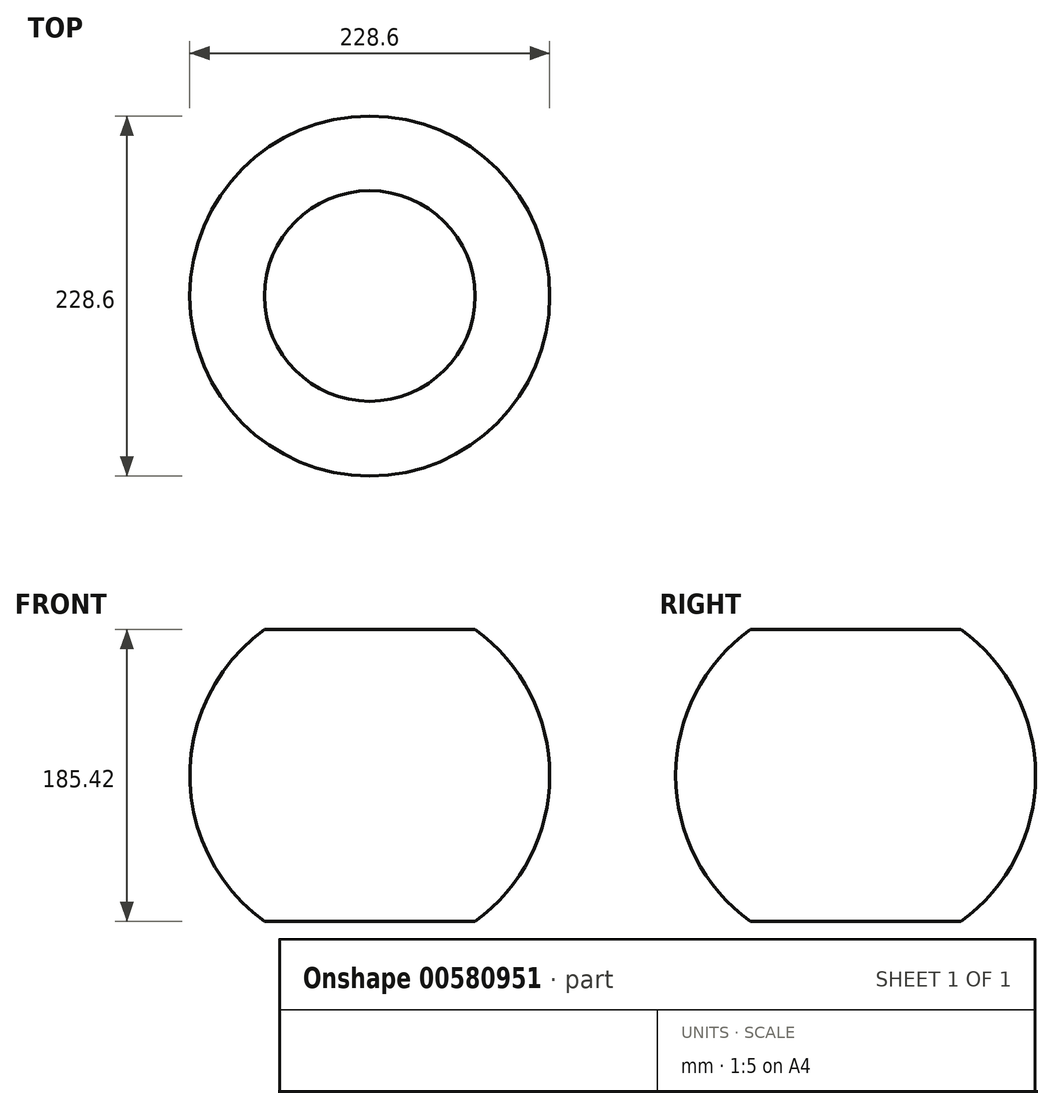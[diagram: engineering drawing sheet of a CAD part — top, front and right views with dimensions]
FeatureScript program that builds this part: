
annotation { "Feature Type Name" : "Feature", "Feature Type Description" : "" }
export const myFeature = defineFeature(function(context is Context, id is Id, definition is map)
    precondition{}
    {
        {
            var Q0;
            Q0=qCreatedBy(makeId("Front.planeOp"),FACE);
            var sketch = newSketch(context, id + "F0", { "sketchPlane" : qUnion([Q0])});
            skArc(sketch, "E0", {"start": v(0, -114.3) * mm, "mid": v(114.3, 0) * mm, "end": v(0, 114.3) * mm});
            skLineSegment(sketch, "E1", {"start": v(0, 114.3) * mm, "end": v(0, -114.3) * mm});
            skSolve(sketch);
        }
        {
            var Q0;
            Q0=makeQuery(id+"F0.imprint","IMPRINT",FACE,{"disambiguationData":[TD([[makeQuery(id+"F0.imprint","IMPRINT",EDGE,{"derivedFrom":sQuery(id+"F0.wireOp",EDGE,"E0")}),1.0]])]});
            var Q1;
            Q1=sQuery(id+"F0.wireOp",EDGE,"E0");
            var Q2;
            Q2=sQuery(id+"F0.wireOp",EDGE,"E1");
            revolve(context, id + "F1", {"entities" : qUnion([Q0]), "surfaceEntities" : qUnion([Q1]), "axis" : qUnion([Q2]), "revolveType" : RevolveType.FULL});
        }
        {
            var Q0;
            Q0=qCreatedBy(makeId("Front.planeOp"),FACE);
            var sketch = newSketch(context, id + "F2", { "sketchPlane" : qUnion([Q0])});
            skLineSegment(sketch, "E2.bottom", {"start": v(-129.8, 129.8) * mm, "end": v(129.8, 129.8) * mm});
            skLineSegment(sketch, "E2.top", {"start": v(-129.8, 92.7) * mm, "end": v(129.8, 92.7) * mm});
            skLineSegment(sketch, "E2.left", {"start": v(-129.8, 129.8) * mm, "end": v(-129.8, 92.7) * mm});
            skLineSegment(sketch, "E2.right", {"start": v(129.8, 129.8) * mm, "end": v(129.8, 92.7) * mm});
            skLineSegment(sketch, "E3.MirrorCS", {"start": v(-129.8, -129.8) * mm, "end": v(129.8, -129.8) * mm});
            skLineSegment(sketch, "E4.MirrorCS", {"start": v(-129.8, -129.8) * mm, "end": v(-129.8, -92.7) * mm});
            skLineSegment(sketch, "E5.MirrorCS", {"start": v(-129.8, -92.7) * mm, "end": v(129.8, -92.7) * mm});
            skLineSegment(sketch, "E6.MirrorCS", {"start": v(129.8, -129.8) * mm, "end": v(129.8, -92.7) * mm});
            skSolve(sketch);
        }
        {
            var Q0;
            Q0=makeQuery(id+"F2.imprint","IMPRINT",FACE,{"disambiguationData":[TD([[makeQuery(id+"F2.imprint","IMPRINT",EDGE,{"derivedFrom":sQuery(id+"F2.wireOp",EDGE,"E2.bottom")}),-1.0]])]});
            var Q1;
            Q1=makeQuery(id+"F2.imprint","IMPRINT",FACE,{"disambiguationData":[TD([[makeQuery(id+"F2.imprint","IMPRINT",EDGE,{"derivedFrom":sQuery(id+"F2.wireOp",EDGE,"E3.MirrorCS")}),1.0]])]});
            extrude(context, id + "F3", {"entities" : qUnion([Q0, Q1]), "operationType" : NewBodyOperationType.REMOVE, "endBound" : BoundingType.THROUGH_ALL, "oppositeDirection" : true, "depth" : 25.4 * mm, "offsetDistance" : 25.4 * mm, "hasSecondDirection" : true, "secondDirectionBound" : SecondDirectionBoundingType.THROUGH_ALL, "secondDirectionOppositeDirection" : false, "secondDirectionDepth" : 25.4 * mm});
        }
    });
